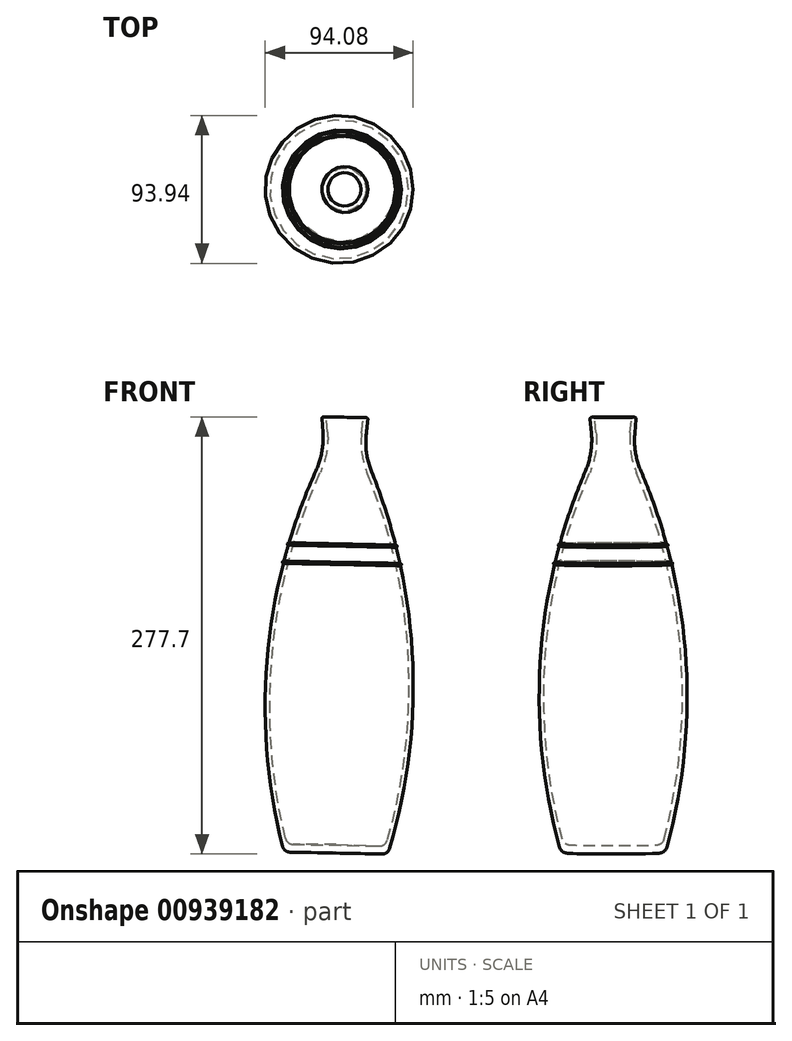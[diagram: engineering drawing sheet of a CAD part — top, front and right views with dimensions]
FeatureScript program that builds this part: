
annotation { "Feature Type Name" : "Feature", "Feature Type Description" : "" }
export const myFeature = defineFeature(function(context is Context, id is Id, definition is map)
    precondition{}
    {
        {
            var Q0;
            Q0=qCreatedBy(makeId("Front.planeOp"),FACE);
            var sketch = newSketch(context, id + "F0", { "sketchPlane" : qUnion([Q0])});
            skLineSegment(sketch, "E0", {"start": v(0, 0) * mm, "end": v(-46, 0) * mm, "construction": true});
            skLineSegment(sketch, "E1.MirrorCS", {"start": v(-2.5, -121.74) * mm, "end": v(-2.6, -126.74) * mm});
            skLineSegment(sketch, "E2", {"start": v(-2.6, -126.74) * mm, "end": v(-31.73, -126.74) * mm});
            skLineSegment(sketch, "E3", {"start": v(-10.93, 139.78) * mm, "end": v(-11.55, 148.69) * mm});
            skPoint(sketch, "E4.visualSharp", {"position": v(-10.02, 126.74) * mm});
            skArc(sketch, "E4.filletArc", {"start": v(-15.26, 115.67) * mm, "mid": v(-11.6, 127.46) * mm, "end": v(-10.93, 139.78) * mm});
            skLineSegment(sketch, "E5", {"start": v(-10.56, 149.76) * mm, "end": v(-9.55, 149.76) * mm});
            skLineSegment(sketch, "E6.0", {"start": v(-2.5, -121.74) * mm, "end": v(-29.87, -121.74) * mm});
            skPoint(sketch, "E7.visualSharp", {"position": v(-33.8, -121.74) * mm});
            skPoint(sketch, "E8.visualSharp", {"position": v(-35.6, -126.74) * mm});
            skLineSegment(sketch, "E9.0", {"start": v(-7.94, 140) * mm, "end": v(-8.56, 148.83) * mm});
            skArc(sketch, "E10.0", {"start": v(-12.72, 114) * mm, "mid": v(-8.69, 126.7) * mm, "end": v(-7.94, 140) * mm});
            skArc(sketch, "E11.filletArc", {"start": v(-36.58, -122.97) * mm, "mid": v(-34.8, -125.69) * mm, "end": v(-31.73, -126.74) * mm});
            skPoint(sketch, "E12.orphan", {"position": v(0, 0) * mm});
            skPoint(sketch, "E13.orphan", {"position": v(-2.6, 126.74) * mm});
            skPoint(sketch, "E14.visualSharp", {"position": v(-11.63, 149.76) * mm});
            skArc(sketch, "E14.filletArc", {"start": v(-10.56, 149.76) * mm, "mid": v(-11.29, 149.44) * mm, "end": v(-11.55, 148.69) * mm});
            skPoint(sketch, "E15.visualSharp", {"position": v(-8.62, 149.76) * mm});
            skArc(sketch, "E15.filletArc", {"start": v(-8.56, 148.83) * mm, "mid": v(-8.87, 149.5) * mm, "end": v(-9.55, 149.76) * mm});
            skArc(sketch, "E16.trimOffspring", {"start": v(-15.26, 115.67) * mm, "mid": v(-46.17, -1.84) * mm, "end": v(-36.58, -122.97) * mm});
            skArc(sketch, "E17.0", {"start": v(-12.53, 114.43) * mm, "mid": v(-42.98, 0.1) * mm, "end": v(-34.73, -117.9) * mm});
            skCircle(sketch, "E18", {"center": v(-35.88, 57.4) * mm, "radius": 0.75 * mm});
            skCircle(sketch, "E19", {"center": v(-32.66, 68.97) * mm, "radius": 0.75 * mm});
            skArc(sketch, "E20.filletArc", {"start": v(-34.73, -117.9) * mm, "mid": v(-32.96, -120.67) * mm, "end": v(-29.87, -121.74) * mm});
            skSolve(sketch);
        }
        {
            var Q0;
            Q0=makeQuery(id+"F0.imprint","IMPRINT",FACE,{"disambiguationData":[TD([[makeQuery(id+"F0.imprint","IMPRINT",EDGE,{"derivedFrom":sQuery(id+"F0.wireOp",EDGE,"E1.MirrorCS")}),-1.0]])]});
            var Q1;
            {var subQ0=sQuery(id+"F0.wireOp",EDGE,"E19");var subQ1=sQuery(id+"F0.wireOp",EDGE,"E16.trimOffspring");var subQ2=makeQuery(id+"F0.imprint","INTERSECT",VERTEX,{"disambiguationData":[OD(0.0)],"derivedFrom":[subQ1,subQ0]});Q1=makeQuery(id+"F0.imprint","IMPRINT",FACE,{"disambiguationData":[TD([[makeQuery(id+"F0.imprint","IMPRINT",EDGE,{"disambiguationData":[TD([[subQ2,-1.0]])],"derivedFrom":subQ1}),-1.0]])]});}
            var Q2;
            {var subQ0=sQuery(id+"F0.wireOp",EDGE,"E18");var subQ1=sQuery(id+"F0.wireOp",EDGE,"E16.trimOffspring");var subQ2=makeQuery(id+"F0.imprint","INTERSECT",VERTEX,{"disambiguationData":[OD(0.0)],"derivedFrom":[subQ1,subQ0]});Q2=makeQuery(id+"F0.imprint","IMPRINT",FACE,{"disambiguationData":[TD([[makeQuery(id+"F0.imprint","IMPRINT",EDGE,{"disambiguationData":[TD([[subQ2,-1.0]])],"derivedFrom":subQ1}),-1.0]])]});}
            var Q3;
            Q3=sQuery(id+"F0.wireOp",EDGE,"E1.MirrorCS");
            revolve(context, id + "F1", {"surfaceOperationType" : NewSurfaceOperationType.NEW, "entities" : qUnion([Q0, Q1, Q2]), "axis" : qUnion([Q3]), "revolveType" : RevolveType.FULL});
        }
    });
